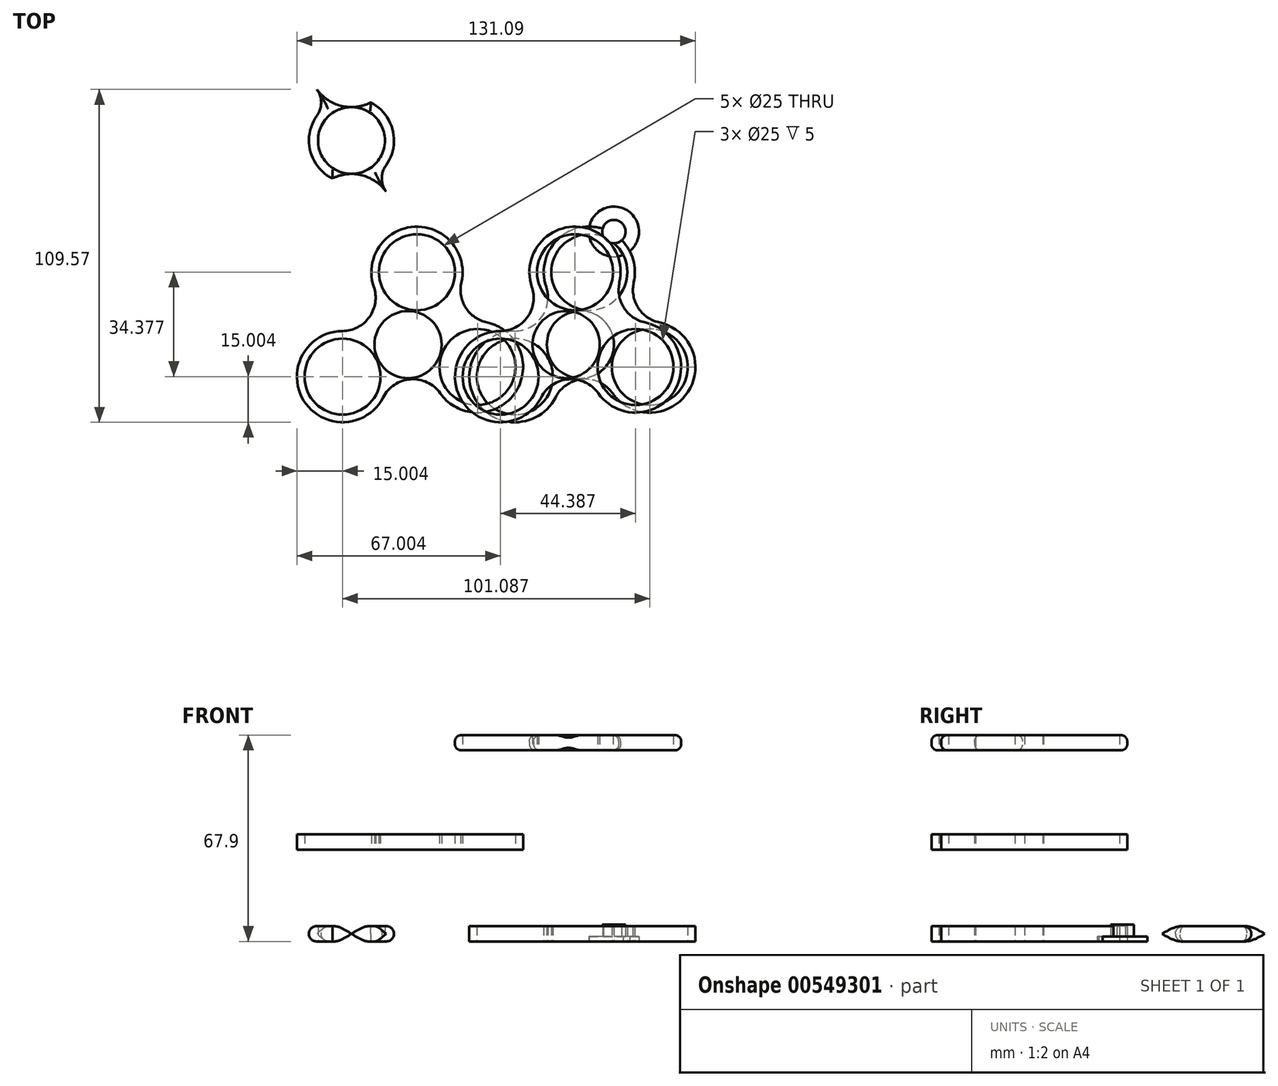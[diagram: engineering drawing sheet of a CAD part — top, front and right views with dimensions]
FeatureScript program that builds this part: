
annotation { "Feature Type Name" : "Feature", "Feature Type Description" : "" }
export const myFeature = defineFeature(function(context is Context, id is Id, definition is map)
    precondition{}
    {
        {
            var Q0;
            Q0=qCreatedBy(makeId("Top.planeOp"),FACE);
            var sketch = newSketch(context, id + "F0", { "sketchPlane" : qUnion([Q0])});
            skCircle(sketch, "E0", {"center": v(15.64, -42.07) * mm, "radius": 39 * mm});
            skCircle(sketch, "E1", {"center": v(15.64, -42.07) * mm, "radius": 11.05 * mm});
            skArc(sketch, "E2", {"start": v(15.64, -3.07) * mm, "mid": v(-17.23, -21.08) * mm, "end": v(-19.75, -58.47) * mm});
            skArc(sketch, "E3", {"start": v(-19.75, -58.47) * mm, "mid": v(14.6, -81.07) * mm, "end": v(50.1, -60.32) * mm});
            skLineSegment(sketch, "E4", {"start": v(-19.75, -58.47) * mm, "end": v(-17.55, -57.2) * mm});
            skLineSegment(sketch, "E5", {"start": v(15.64, -3.07) * mm, "end": v(16.72, -5.89) * mm});
            skLineSegment(sketch, "E6", {"start": v(50.1, -60.32) * mm, "end": v(47.05, -58.56) * mm});
            skCircle(sketch, "E7", {"center": v(18.57, -18.25) * mm, "radius": 12.5 * mm});
            skCircle(sketch, "E8", {"center": v(-5.92, -52.63) * mm, "radius": 12.5 * mm});
            skCircle(sketch, "E9", {"center": v(38.47, -49.46) * mm, "radius": 12.5 * mm});
            skCircle(sketch, "E10", {"center": v(18.57, -18.25) * mm, "radius": 15 * mm});
            skCircle(sketch, "E11", {"center": v(-5.92, -52.63) * mm, "radius": 15 * mm});
            skCircle(sketch, "E12", {"center": v(38.47, -49.46) * mm, "radius": 15 * mm});
            skPoint(sketch, "E13", {"position": v(15.64, -53.57) * mm});
            skPoint(sketch, "E14", {"position": v(3.28, -32.48) * mm});
            skPoint(sketch, "E15", {"position": v(34.2, -29.18) * mm});
            skArc(sketch, "E16", {"start": v(33.2, -21.6) * mm, "mid": v(34.64, -29.95) * mm, "end": v(41.6, -34.8) * mm});
            skArc(sketch, "E17", {"start": v(-5.98, -37.63) * mm, "mid": v(2.92, -33.01) * mm, "end": v(4.37, -23.09) * mm});
            skArc(sketch, "E18", {"start": v(26.21, -58.1) * mm, "mid": v(16.45, -53.48) * mm, "end": v(7.44, -59.45) * mm});
            skSolve(sketch);
        }
        {
            var Q0;
            {var subQ5=sQuery(id+"F0.wireOp",EDGE,"E16");Q0=makeQuery(id+"F0.imprint","IMPRINT",FACE,{"disambiguationData":[TD([[makeQuery(id+"F0.imprint","IMPRINT",EDGE,{"derivedFrom":subQ5}),-1.0]])]});}
            var Q1;
            Q1=makeQuery(id+"F0.imprint","IMPRINT",FACE,{"disambiguationData":[TD([[makeQuery(id+"F0.imprint","IMPRINT",EDGE,{"derivedFrom":sQuery(id+"F0.wireOp",EDGE,"E9")}),-1.0]])]});
            var Q2;
            {var subQ5=sQuery(id+"F0.wireOp",EDGE,"E18");Q2=makeQuery(id+"F0.imprint","IMPRINT",FACE,{"disambiguationData":[TD([[makeQuery(id+"F0.imprint","IMPRINT",EDGE,{"derivedFrom":subQ5}),-1.0]])]});}
            var Q3;
            Q3=makeQuery(id+"F0.imprint","IMPRINT",FACE,{"disambiguationData":[TD([[makeQuery(id+"F0.imprint","IMPRINT",EDGE,{"derivedFrom":sQuery(id+"F0.wireOp",EDGE,"E8")}),-1.0]])]});
            var Q4;
            {var subQ5=sQuery(id+"F0.wireOp",EDGE,"E17");Q4=makeQuery(id+"F0.imprint","IMPRINT",FACE,{"disambiguationData":[TD([[makeQuery(id+"F0.imprint","IMPRINT",EDGE,{"derivedFrom":subQ5}),-1.0]])]});}
            var Q5;
            Q5=makeQuery(id+"F0.imprint","IMPRINT",FACE,{"disambiguationData":[TD([[makeQuery(id+"F0.imprint","IMPRINT",EDGE,{"derivedFrom":sQuery(id+"F0.wireOp",EDGE,"E7")}),-1.0]])]});
            extrude(context, id + "F1", {"entities" : qUnion([Q0, Q1, Q2, Q3, Q4, Q5]), "depth" : 5 * mm, "offsetDistance" : 25 * mm});
        }
        {
            var Q0;
            Q0=qCreatedBy(makeId("Top.planeOp"),FACE);
            var sketch = newSketch(context, id + "F2", { "sketchPlane" : qUnion([Q0])});
            skLineSegment(sketch, "E19", {"start": v(-59.68, 64.11) * mm, "end": v(-59.68, -13.89) * mm});
            skLineSegment(sketch, "E20", {"start": v(-59.68, 64.11) * mm, "end": v(-59.68, 61.11) * mm});
            skLineSegment(sketch, "E21", {"start": v(-59.68, 61.11) * mm, "end": v(-59.68, 39.11) * mm});
            skLineSegment(sketch, "E22", {"start": v(-59.68, 39.11) * mm, "end": v(-59.68, 36.11) * mm});
            skLineSegment(sketch, "E23", {"start": v(-59.68, 36.11) * mm, "end": v(-59.68, 14.11) * mm});
            skLineSegment(sketch, "E24", {"start": v(-59.68, 14.11) * mm, "end": v(-59.68, 11.11) * mm});
            skLineSegment(sketch, "E25", {"start": v(-59.68, 11.11) * mm, "end": v(-59.68, -10.89) * mm});
            skLineSegment(sketch, "E26", {"start": v(-59.68, -10.89) * mm, "end": v(-59.68, -13.89) * mm});
            skCircle(sketch, "E27", {"center": v(-59.68, 25.11) * mm, "radius": 11 * mm});
            skCircle(sketch, "E28", {"center": v(-59.68, 0.11) * mm, "radius": 14 * mm});
            skCircle(sketch, "E29", {"center": v(-59.68, 25.11) * mm, "radius": 14 * mm});
            skCircle(sketch, "E30", {"center": v(-59.68, 50.11) * mm, "radius": 14 * mm});
            skArc(sketch, "E31", {"start": v(-48.31, 16.94) * mm, "mid": v(-49.7, 12.61) * mm, "end": v(-48.31, 8.28) * mm});
            skArc(sketch, "E32.MirrorCS", {"start": v(-71.05, 16.94) * mm, "mid": v(-69.66, 12.61) * mm, "end": v(-71.05, 8.28) * mm});
            skLineSegment(sketch, "E33", {"start": v(-70.68, 25.11) * mm, "end": v(-48.68, 25.11) * mm});
            skArc(sketch, "E34.MirrorCS", {"start": v(-48.31, 33.28) * mm, "mid": v(-49.7, 37.61) * mm, "end": v(-48.31, 41.94) * mm});
            skArc(sketch, "E35.MirrorCS", {"start": v(-71.05, 33.28) * mm, "mid": v(-69.66, 37.61) * mm, "end": v(-71.05, 41.94) * mm});
            skSolve(sketch);
        }
        {
            var Q0;
            {var subQ7=sQuery(id+"F2.wireOp",EDGE,"E20");Q0=makeQuery(id+"F2.imprint","IMPRINT",FACE,{"disambiguationData":[TD([[makeQuery(id+"F2.imprint","IMPRINT",EDGE,{"derivedFrom":subQ7}),1.0]])]});}
            var Q1;
            {var subQ0=sQuery(id+"F2.wireOp",EDGE,"E35.MirrorCS");Q1=makeQuery(id+"F2.imprint","IMPRINT",FACE,{"disambiguationData":[TD([[makeQuery(id+"F2.imprint","IMPRINT",EDGE,{"derivedFrom":subQ0}),-1.0]])]});}
            var Q2;
            {var subQ1=sQuery(id+"F2.wireOp",EDGE,"E20");Q2=makeQuery(id+"F2.imprint","IMPRINT",FACE,{"disambiguationData":[TD([[makeQuery(id+"F2.imprint","IMPRINT",EDGE,{"derivedFrom":subQ1}),-1.0]])]});}
            var Q3;
            {var subQ0=sQuery(id+"F2.wireOp",EDGE,"E22");Q3=makeQuery(id+"F2.imprint","IMPRINT",FACE,{"disambiguationData":[TD([[makeQuery(id+"F2.imprint","IMPRINT",EDGE,{"derivedFrom":subQ0}),-1.0]])]});}
            var Q4;
            {var subQ0=sQuery(id+"F2.wireOp",EDGE,"E22");Q4=makeQuery(id+"F2.imprint","IMPRINT",FACE,{"disambiguationData":[TD([[makeQuery(id+"F2.imprint","IMPRINT",EDGE,{"derivedFrom":subQ0}),1.0]])]});}
            var Q5;
            {var subQ0=sQuery(id+"F2.wireOp",EDGE,"E29");var subQ1=makeQuery(id+"F2.imprint","INTERSECT",VERTEX,{"derivedFrom":[subQ0,sQuery(id+"F2.wireOp",EDGE,"E34.MirrorCS")]});Q5=makeQuery(id+"F2.imprint","IMPRINT",FACE,{"disambiguationData":[TD([[makeQuery(id+"F2.imprint","IMPRINT",EDGE,{"disambiguationData":[TD([[subQ1,-1.0]])],"derivedFrom":subQ0}),1.0]])]});}
            var Q6;
            {var subQ0=sQuery(id+"F2.wireOp",EDGE,"E34.MirrorCS");Q6=makeQuery(id+"F2.imprint","IMPRINT",FACE,{"disambiguationData":[TD([[makeQuery(id+"F2.imprint","IMPRINT",EDGE,{"derivedFrom":subQ0}),1.0]])]});}
            var Q7;
            {var subQ0=sQuery(id+"F2.wireOp",EDGE,"E29");var subQ1=makeQuery(id+"F2.imprint","INTERSECT",VERTEX,{"derivedFrom":[subQ0,sQuery(id+"F2.wireOp",EDGE,"E35.MirrorCS")]});Q7=makeQuery(id+"F2.imprint","IMPRINT",FACE,{"disambiguationData":[TD([[makeQuery(id+"F2.imprint","IMPRINT",EDGE,{"disambiguationData":[TD([[subQ1,1.0]])],"derivedFrom":subQ0}),1.0]])]});}
            var Q8;
            {var subQ0=sQuery(id+"F2.wireOp",EDGE,"E24");Q8=makeQuery(id+"F2.imprint","IMPRINT",FACE,{"disambiguationData":[TD([[makeQuery(id+"F2.imprint","IMPRINT",EDGE,{"derivedFrom":subQ0}),-1.0]])]});}
            var Q9;
            {var subQ0=sQuery(id+"F2.wireOp",EDGE,"E24");Q9=makeQuery(id+"F2.imprint","IMPRINT",FACE,{"disambiguationData":[TD([[makeQuery(id+"F2.imprint","IMPRINT",EDGE,{"derivedFrom":subQ0}),1.0]])]});}
            var Q10;
            {var subQ0=sQuery(id+"F2.wireOp",EDGE,"E31");Q10=makeQuery(id+"F2.imprint","IMPRINT",FACE,{"disambiguationData":[TD([[makeQuery(id+"F2.imprint","IMPRINT",EDGE,{"derivedFrom":subQ0}),-1.0]])]});}
            var Q11;
            {var subQ1=sQuery(id+"F2.wireOp",EDGE,"E26");Q11=makeQuery(id+"F2.imprint","IMPRINT",FACE,{"disambiguationData":[TD([[makeQuery(id+"F2.imprint","IMPRINT",EDGE,{"derivedFrom":subQ1}),1.0]])]});}
            var Q12;
            {var subQ0=sQuery(id+"F2.wireOp",EDGE,"E32.MirrorCS");Q12=makeQuery(id+"F2.imprint","IMPRINT",FACE,{"disambiguationData":[TD([[makeQuery(id+"F2.imprint","IMPRINT",EDGE,{"derivedFrom":subQ0}),1.0]])]});}
            var Q13;
            {var subQ1=sQuery(id+"F2.wireOp",EDGE,"E26");Q13=makeQuery(id+"F2.imprint","IMPRINT",FACE,{"disambiguationData":[TD([[makeQuery(id+"F2.imprint","IMPRINT",EDGE,{"derivedFrom":subQ1}),-1.0]])]});}
            extrude(context, id + "F3", {"entities" : qUnion([Q0, Q1, Q2, Q3, Q4, Q5, Q6, Q7, Q8, Q9, Q10, Q11, Q12, Q13]), "depth" : 5 * mm, "offsetDistance" : 25 * mm});
        }
        {
            var Q0;
            Q0=makeQuery(id+"F3.opExtrude","CAP_EDGE",EDGE,{"disambiguationData":[OSD([sQuery(id+"F2.wireOp",EDGE,"E30")])],"isStart":false});
            var Q1;
            Q1=makeQuery(id+"F3.opExtrude","CAP_EDGE",EDGE,{"disambiguationData":[OSD([sQuery(id+"F2.wireOp",EDGE,"E35.MirrorCS")])],"isStart":false});
            var Q2;
            {var subQ0=sQuery(id+"F2.wireOp",EDGE,"E29");Q2=makeQuery(id+"F3.opExtrude","CAP_EDGE",EDGE,{"disambiguationData":[OSD([subQ0]),TDD([makeQuery(id+"F2.imprint","IMPRINT",EDGE,{"disambiguationData":[TD([[makeQuery(id+"F2.imprint","INTERSECT",VERTEX,{"derivedFrom":[subQ0,sQuery(id+"F2.wireOp",EDGE,"E32.MirrorCS")]}),1.0]])],"derivedFrom":subQ0})])],"isStart":false});}
            var Q3;
            Q3=makeQuery(id+"F3.opExtrude","CAP_EDGE",EDGE,{"disambiguationData":[OSD([sQuery(id+"F2.wireOp",EDGE,"E30")])],"isStart":true});
            var Q4;
            {var subQ0=sQuery(id+"F2.wireOp",EDGE,"E29");Q4=makeQuery(id+"F3.opExtrude","CAP_EDGE",EDGE,{"disambiguationData":[OSD([subQ0]),TDD([makeQuery(id+"F2.imprint","IMPRINT",EDGE,{"disambiguationData":[TD([[makeQuery(id+"F2.imprint","INTERSECT",VERTEX,{"derivedFrom":[subQ0,sQuery(id+"F2.wireOp",EDGE,"E31")]}),-1.0]])],"derivedFrom":subQ0})])],"isStart":true});}
            var Q5;
            Q5=makeQuery(id+"F3.opExtrude","CAP_EDGE",EDGE,{"disambiguationData":[OSD([sQuery(id+"F2.wireOp",EDGE,"E31")])],"isStart":true});
            var Q6;
            Q6=makeQuery(id+"F3.opExtrude","CAP_EDGE",EDGE,{"disambiguationData":[OSD([sQuery(id+"F2.wireOp",EDGE,"E28")])],"isStart":true});
            var Q7;
            Q7=makeQuery(id+"F3.opExtrude","CAP_EDGE",EDGE,{"disambiguationData":[OSD([sQuery(id+"F2.wireOp",EDGE,"E32.MirrorCS")])],"isStart":true});
            var Q8;
            {var subQ0=sQuery(id+"F2.wireOp",EDGE,"E29");Q8=makeQuery(id+"F3.opExtrude","CAP_EDGE",EDGE,{"disambiguationData":[OSD([subQ0]),TDD([makeQuery(id+"F2.imprint","IMPRINT",EDGE,{"disambiguationData":[TD([[makeQuery(id+"F2.imprint","INTERSECT",VERTEX,{"derivedFrom":[subQ0,sQuery(id+"F2.wireOp",EDGE,"E32.MirrorCS")]}),1.0]])],"derivedFrom":subQ0})])],"isStart":true});}
            var Q9;
            Q9=makeQuery(id+"F3.opExtrude","CAP_EDGE",EDGE,{"disambiguationData":[OSD([sQuery(id+"F2.wireOp",EDGE,"E35.MirrorCS")])],"isStart":true});
            var Q10;
            Q10=makeQuery(id+"F3.opExtrude","CAP_EDGE",EDGE,{"disambiguationData":[OSD([sQuery(id+"F2.wireOp",EDGE,"E34.MirrorCS")])],"isStart":true});
            var Q11;
            Q11=makeQuery(id+"F3.opExtrude","CAP_EDGE",EDGE,{"disambiguationData":[OSD([sQuery(id+"F2.wireOp",EDGE,"E34.MirrorCS")])],"isStart":false});
            var Q12;
            {var subQ0=sQuery(id+"F2.wireOp",EDGE,"E29");Q12=makeQuery(id+"F3.opExtrude","CAP_EDGE",EDGE,{"disambiguationData":[OSD([subQ0]),TDD([makeQuery(id+"F2.imprint","IMPRINT",EDGE,{"disambiguationData":[TD([[makeQuery(id+"F2.imprint","INTERSECT",VERTEX,{"derivedFrom":[subQ0,sQuery(id+"F2.wireOp",EDGE,"E31")]}),-1.0]])],"derivedFrom":subQ0})])],"isStart":false});}
            var Q13;
            Q13=makeQuery(id+"F3.opExtrude","CAP_EDGE",EDGE,{"disambiguationData":[OSD([sQuery(id+"F2.wireOp",EDGE,"E31")])],"isStart":false});
            var Q14;
            Q14=makeQuery(id+"F3.opExtrude","CAP_EDGE",EDGE,{"disambiguationData":[OSD([sQuery(id+"F2.wireOp",EDGE,"E28")])],"isStart":false});
            var Q15;
            Q15=makeQuery(id+"F3.opExtrude","CAP_EDGE",EDGE,{"disambiguationData":[OSD([sQuery(id+"F2.wireOp",EDGE,"E32.MirrorCS")])],"isStart":false});
            fillet(context, id + "F4", {"entities" : qUnion([Q0, Q1, Q2, Q3, Q4, Q5, Q6, Q7, Q8, Q9, Q10, Q11, Q12, Q13, Q14, Q15]), "radius" : 2.5 * mm, "tangentPropagation" : true, "allowEdgeOverflow" : false});
        }
        {
            var Q0;
            Q0=makeQuery(id+"F1.opExtrude","SWEPT_BODY",BODY,{"disambiguationData":[OSD([sQuery(id+"F0.wireOp",EDGE,"E1"),sQuery(id+"F0.wireOp",EDGE,"E7"),sQuery(id+"F0.wireOp",EDGE,"E8"),sQuery(id+"F0.wireOp",EDGE,"E9"),sQuery(id+"F0.wireOp",EDGE,"E10"),sQuery(id+"F0.wireOp",EDGE,"E11"),sQuery(id+"F0.wireOp",EDGE,"E12"),sQuery(id+"F0.wireOp",EDGE,"E16"),sQuery(id+"F0.wireOp",EDGE,"E17"),sQuery(id+"F0.wireOp",EDGE,"E18")])]});
            transform(context, id + "F5", {"entities" : qUnion([Q0]), "transformType" : TransformType.TRANSLATION_3D, "dx" : -4.7 * mm, "dy" : 0 * mm, "dz" : 62.9 * mm, "makeCopy" : true});
        }
        {
            var Q0;
            Q0=makeQuery(id+"F5.opPattern","COPY",BODY,{"derivedFrom":makeQuery(id+"F1.opExtrude","SWEPT_BODY",BODY,{"disambiguationData":[OSD([sQuery(id+"F0.wireOp",EDGE,"E1"),sQuery(id+"F0.wireOp",EDGE,"E7"),sQuery(id+"F0.wireOp",EDGE,"E8"),sQuery(id+"F0.wireOp",EDGE,"E9"),sQuery(id+"F0.wireOp",EDGE,"E10"),sQuery(id+"F0.wireOp",EDGE,"E11"),sQuery(id+"F0.wireOp",EDGE,"E12"),sQuery(id+"F0.wireOp",EDGE,"E16"),sQuery(id+"F0.wireOp",EDGE,"E17"),sQuery(id+"F0.wireOp",EDGE,"E18")])]}),"instanceName":"1"});
            transform(context, id + "F6", {"entities" : qUnion([Q0]), "transformType" : TransformType.TRANSLATION_3D, "dx" : -52 * mm, "dy" : 0 * mm, "dz" : -32.7 * mm, "makeCopy" : true});
        }
        {
            var Q0;
            Q0=qCreatedBy(makeId("Top.planeOp"),FACE);
            var sketch = newSketch(context, id + "F7", { "sketchPlane" : qUnion([Q0])});
            skCircle(sketch, "E36", {"center": v(26.66, -4.88) * mm, "radius": 8.25 * mm});
            skSolve(sketch);
        }
        {
            var Q0;
            Q0=makeQuery(id+"F7.imprint","IMPRINT",FACE,{"disambiguationData":[TD([[makeQuery(id+"F7.imprint","IMPRINT",EDGE,{"derivedFrom":sQuery(id+"F7.wireOp",EDGE,"E36")}),1.0]])]});
            extrude(context, id + "F8", {"entities" : qUnion([Q0]), "depth" : 1.64 * mm, "offsetDistance" : 25 * mm});
        }
        {
            var Q0;
            Q0=makeQuery(id+"F8.opExtrude","CAP_FACE",FACE,{"disambiguationData":[OSD([sQuery(id+"F7.wireOp",EDGE,"E36")])],"isStart":false});
            var sketch = newSketch(context, id + "F9", { "sketchPlane" : qUnion([Q0])});
            skCircle(sketch, "E37", {"center": v(26.66, -4.88) * mm, "radius": 3.84 * mm});
            skSolve(sketch);
        }
        {
            var Q0;
            Q0=makeQuery(id+"F9.imprint","IMPRINT",FACE,{"disambiguationData":[TD([[makeQuery(id+"F9.imprint","IMPRINT",EDGE,{"derivedFrom":sQuery(id+"F9.wireOp",EDGE,"E37")}),1.0]])]});
            extrude(context, id + "F10", {"entities" : qUnion([Q0]), "operationType" : NewBodyOperationType.ADD, "depth" : 3.9 * mm, "offsetDistance" : 25 * mm});
        }
        {
            var Q0;
            Q0=makeQuery(id+"F3.opExtrude","CAP_FACE",FACE,{"disambiguationData":[OSD([sQuery(id+"F2.wireOp",EDGE,"E27"),sQuery(id+"F2.wireOp",EDGE,"E28"),sQuery(id+"F2.wireOp",EDGE,"E29"),sQuery(id+"F2.wireOp",EDGE,"E30"),sQuery(id+"F2.wireOp",EDGE,"E31"),sQuery(id+"F2.wireOp",EDGE,"E32.MirrorCS"),sQuery(id+"F2.wireOp",EDGE,"E34.MirrorCS"),sQuery(id+"F2.wireOp",EDGE,"E35.MirrorCS")])],"isStart":false});
            var sketch = newSketch(context, id + "F11", { "sketchPlane" : qUnion([Q0])});
            skLineSegment(sketch, "E38", {"start": v(-59.97, -1.73) * mm, "end": v(-62.66, -1.73) * mm});
            skLineSegment(sketch, "E39", {"start": v(-62.66, -1.73) * mm, "end": v(-62.7, -1.73) * mm});
            skLineSegment(sketch, "E40", {"start": v(-62.7, -1.73) * mm, "end": v(-62.8, -1.76) * mm});
            skLineSegment(sketch, "E41", {"start": v(-62.8, -1.76) * mm, "end": v(-62.93, -1.84) * mm});
            skLineSegment(sketch, "E42", {"start": v(-62.93, -1.84) * mm, "end": v(-63, -1.95) * mm});
            skLineSegment(sketch, "E43", {"start": v(-63, -1.95) * mm, "end": v(-63.04, -2.06) * mm});
            skLineSegment(sketch, "E44", {"start": v(-63.04, -2.06) * mm, "end": v(-63.04, -2.1) * mm});
            skLineSegment(sketch, "E45", {"start": v(-63.04, -2.1) * mm, "end": v(-63.04, -2.14) * mm});
            skLineSegment(sketch, "E46", {"start": v(-63.04, -2.14) * mm, "end": v(-63, -2.24) * mm});
            skLineSegment(sketch, "E47", {"start": v(-63, -2.24) * mm, "end": v(-62.93, -2.36) * mm});
            skLineSegment(sketch, "E48", {"start": v(-62.93, -2.36) * mm, "end": v(-62.8, -2.44) * mm});
            skLineSegment(sketch, "E49", {"start": v(-62.8, -2.44) * mm, "end": v(-62.7, -2.47) * mm});
            skLineSegment(sketch, "E50", {"start": v(-62.7, -2.47) * mm, "end": v(-62.66, -2.47) * mm});
            skLineSegment(sketch, "E51", {"start": v(-62.66, -2.47) * mm, "end": v(-59.97, -2.47) * mm});
            skLineSegment(sketch, "E52", {"start": v(-59.97, -2.47) * mm, "end": v(-59.93, -2.47) * mm});
            skLineSegment(sketch, "E53", {"start": v(-59.93, -2.47) * mm, "end": v(-59.82, -2.44) * mm});
            skLineSegment(sketch, "E54", {"start": v(-59.82, -2.44) * mm, "end": v(-59.7, -2.36) * mm});
            skLineSegment(sketch, "E55", {"start": v(-59.7, -2.36) * mm, "end": v(-59.63, -2.24) * mm});
            skLineSegment(sketch, "E56", {"start": v(-59.63, -2.24) * mm, "end": v(-59.6, -2.14) * mm});
            skLineSegment(sketch, "E57", {"start": v(-59.6, -2.14) * mm, "end": v(-59.6, -2.1) * mm});
            skLineSegment(sketch, "E58", {"start": v(-59.6, -2.1) * mm, "end": v(-59.6, -2.06) * mm});
            skLineSegment(sketch, "E59", {"start": v(-59.6, -2.06) * mm, "end": v(-59.63, -1.95) * mm});
            skLineSegment(sketch, "E60", {"start": v(-59.63, -1.95) * mm, "end": v(-59.7, -1.84) * mm});
            skLineSegment(sketch, "E61", {"start": v(-59.7, -1.84) * mm, "end": v(-59.82, -1.76) * mm});
            skLineSegment(sketch, "E62", {"start": v(-59.82, -1.76) * mm, "end": v(-59.93, -1.73) * mm});
            skLineSegment(sketch, "E63", {"start": v(-59.93, -1.73) * mm, "end": v(-59.97, -1.73) * mm});
            skLineSegment(sketch, "E64", {"start": v(-58.26, -0.47) * mm, "end": v(-62.14, -0.47) * mm});
            skLineSegment(sketch, "E65", {"start": v(-62.14, -0.47) * mm, "end": v(-62.17, -0.47) * mm});
            skLineSegment(sketch, "E66", {"start": v(-62.17, -0.47) * mm, "end": v(-62.28, -0.5) * mm});
            skLineSegment(sketch, "E67", {"start": v(-62.28, -0.5) * mm, "end": v(-62.4, -0.58) * mm});
            skLineSegment(sketch, "E68", {"start": v(-62.4, -0.58) * mm, "end": v(-62.48, -0.7) * mm});
            skLineSegment(sketch, "E69", {"start": v(-62.48, -0.7) * mm, "end": v(-62.5, -0.8) * mm});
            skLineSegment(sketch, "E70", {"start": v(-62.5, -0.8) * mm, "end": v(-62.5, -0.84) * mm});
            skLineSegment(sketch, "E71", {"start": v(-62.5, -0.84) * mm, "end": v(-62.5, -0.88) * mm});
            skLineSegment(sketch, "E72", {"start": v(-62.5, -0.88) * mm, "end": v(-62.48, -0.98) * mm});
            skLineSegment(sketch, "E73", {"start": v(-62.48, -0.98) * mm, "end": v(-62.4, -1.1) * mm});
            skLineSegment(sketch, "E74", {"start": v(-62.4, -1.1) * mm, "end": v(-62.28, -1.18) * mm});
            skLineSegment(sketch, "E75", {"start": v(-62.28, -1.18) * mm, "end": v(-62.17, -1.21) * mm});
            skLineSegment(sketch, "E76", {"start": v(-62.17, -1.21) * mm, "end": v(-62.14, -1.21) * mm});
            skLineSegment(sketch, "E77", {"start": v(-62.14, -1.21) * mm, "end": v(-58.26, -1.21) * mm});
            skLineSegment(sketch, "E78", {"start": v(-58.26, -1.21) * mm, "end": v(-58.22, -1.21) * mm});
            skLineSegment(sketch, "E79", {"start": v(-58.22, -1.21) * mm, "end": v(-58.11, -1.18) * mm});
            skLineSegment(sketch, "E80", {"start": v(-58.11, -1.18) * mm, "end": v(-58, -1.1) * mm});
            skLineSegment(sketch, "E81", {"start": v(-58, -1.1) * mm, "end": v(-57.91, -0.98) * mm});
            skLineSegment(sketch, "E82", {"start": v(-57.91, -0.98) * mm, "end": v(-57.88, -0.88) * mm});
            skLineSegment(sketch, "E83", {"start": v(-57.88, -0.88) * mm, "end": v(-57.88, -0.84) * mm});
            skLineSegment(sketch, "E84", {"start": v(-57.88, -0.84) * mm, "end": v(-57.88, -0.8) * mm});
            skLineSegment(sketch, "E85", {"start": v(-57.88, -0.8) * mm, "end": v(-57.91, -0.7) * mm});
            skLineSegment(sketch, "E86", {"start": v(-57.91, -0.7) * mm, "end": v(-58, -0.58) * mm});
            skLineSegment(sketch, "E87", {"start": v(-58, -0.58) * mm, "end": v(-58.11, -0.5) * mm});
            skLineSegment(sketch, "E88", {"start": v(-58.11, -0.5) * mm, "end": v(-58.22, -0.47) * mm});
            skLineSegment(sketch, "E89", {"start": v(-58.22, -0.47) * mm, "end": v(-58.26, -0.47) * mm});
            skLineSegment(sketch, "E90", {"start": v(-57.47, 0.8) * mm, "end": v(-62.14, 0.8) * mm});
            skLineSegment(sketch, "E91", {"start": v(-62.14, 0.8) * mm, "end": v(-62.17, 0.8) * mm});
            skLineSegment(sketch, "E92", {"start": v(-62.17, 0.8) * mm, "end": v(-62.28, 0.76) * mm});
            skLineSegment(sketch, "E93", {"start": v(-62.28, 0.76) * mm, "end": v(-62.4, 0.68) * mm});
            skLineSegment(sketch, "E94", {"start": v(-62.4, 0.68) * mm, "end": v(-62.48, 0.57) * mm});
            skLineSegment(sketch, "E95", {"start": v(-62.48, 0.57) * mm, "end": v(-62.5, 0.46) * mm});
            skLineSegment(sketch, "E96", {"start": v(-62.5, 0.46) * mm, "end": v(-62.5, 0.42) * mm});
            skLineSegment(sketch, "E97", {"start": v(-62.5, 0.42) * mm, "end": v(-62.5, 0.38) * mm});
            skLineSegment(sketch, "E98", {"start": v(-62.5, 0.38) * mm, "end": v(-62.48, 0.28) * mm});
            skLineSegment(sketch, "E99", {"start": v(-62.48, 0.28) * mm, "end": v(-62.4, 0.16) * mm});
            skLineSegment(sketch, "E100", {"start": v(-62.4, 0.16) * mm, "end": v(-62.28, 0.08) * mm});
            skLineSegment(sketch, "E101", {"start": v(-62.28, 0.08) * mm, "end": v(-62.17, 0.05) * mm});
            skLineSegment(sketch, "E102", {"start": v(-62.17, 0.05) * mm, "end": v(-62.14, 0.05) * mm});
            skLineSegment(sketch, "E103", {"start": v(-62.14, 0.05) * mm, "end": v(-57.47, 0.05) * mm});
            skLineSegment(sketch, "E104", {"start": v(-57.47, 0.05) * mm, "end": v(-57.43, 0.05) * mm});
            skLineSegment(sketch, "E105", {"start": v(-57.43, 0.05) * mm, "end": v(-57.32, 0.08) * mm});
            skLineSegment(sketch, "E106", {"start": v(-57.32, 0.08) * mm, "end": v(-57.2, 0.16) * mm});
            skLineSegment(sketch, "E107", {"start": v(-57.2, 0.16) * mm, "end": v(-57.13, 0.28) * mm});
            skLineSegment(sketch, "E108", {"start": v(-57.13, 0.28) * mm, "end": v(-57.1, 0.38) * mm});
            skLineSegment(sketch, "E109", {"start": v(-57.1, 0.38) * mm, "end": v(-57.1, 0.42) * mm});
            skLineSegment(sketch, "E110", {"start": v(-57.1, 0.42) * mm, "end": v(-57.1, 0.46) * mm});
            skLineSegment(sketch, "E111", {"start": v(-57.1, 0.46) * mm, "end": v(-57.13, 0.57) * mm});
            skLineSegment(sketch, "E112", {"start": v(-57.13, 0.57) * mm, "end": v(-57.2, 0.68) * mm});
            skLineSegment(sketch, "E113", {"start": v(-57.2, 0.68) * mm, "end": v(-57.32, 0.76) * mm});
            skLineSegment(sketch, "E114", {"start": v(-57.32, 0.76) * mm, "end": v(-57.43, 0.8) * mm});
            skLineSegment(sketch, "E115", {"start": v(-57.43, 0.8) * mm, "end": v(-57.47, 0.8) * mm});
            skLineSegment(sketch, "E116", {"start": v(-58.11, 2.05) * mm, "end": v(-62.14, 2.05) * mm});
            skLineSegment(sketch, "E117", {"start": v(-62.14, 2.05) * mm, "end": v(-62.17, 2.05) * mm});
            skLineSegment(sketch, "E118", {"start": v(-62.17, 2.05) * mm, "end": v(-62.28, 2.02) * mm});
            skLineSegment(sketch, "E119", {"start": v(-62.28, 2.02) * mm, "end": v(-62.4, 1.94) * mm});
            skLineSegment(sketch, "E120", {"start": v(-62.4, 1.94) * mm, "end": v(-62.48, 1.82) * mm});
            skLineSegment(sketch, "E121", {"start": v(-62.48, 1.82) * mm, "end": v(-62.5, 1.72) * mm});
            skLineSegment(sketch, "E122", {"start": v(-62.5, 1.72) * mm, "end": v(-62.5, 1.68) * mm});
            skLineSegment(sketch, "E123", {"start": v(-62.5, 1.68) * mm, "end": v(-62.5, 1.64) * mm});
            skLineSegment(sketch, "E124", {"start": v(-62.5, 1.64) * mm, "end": v(-62.48, 1.53) * mm});
            skLineSegment(sketch, "E125", {"start": v(-62.48, 1.53) * mm, "end": v(-62.4, 1.42) * mm});
            skLineSegment(sketch, "E126", {"start": v(-62.4, 1.42) * mm, "end": v(-62.28, 1.34) * mm});
            skLineSegment(sketch, "E127", {"start": v(-62.28, 1.34) * mm, "end": v(-62.17, 1.3) * mm});
            skLineSegment(sketch, "E128", {"start": v(-62.17, 1.3) * mm, "end": v(-62.14, 1.3) * mm});
            skLineSegment(sketch, "E129", {"start": v(-62.14, 1.3) * mm, "end": v(-58.11, 1.3) * mm});
            skLineSegment(sketch, "E130", {"start": v(-58.11, 1.3) * mm, "end": v(-58.08, 1.3) * mm});
            skLineSegment(sketch, "E131", {"start": v(-58.08, 1.3) * mm, "end": v(-57.97, 1.34) * mm});
            skLineSegment(sketch, "E132", {"start": v(-57.97, 1.34) * mm, "end": v(-57.85, 1.42) * mm});
            skLineSegment(sketch, "E133", {"start": v(-57.85, 1.42) * mm, "end": v(-57.77, 1.53) * mm});
            skLineSegment(sketch, "E134", {"start": v(-57.77, 1.53) * mm, "end": v(-57.74, 1.64) * mm});
            skLineSegment(sketch, "E135", {"start": v(-57.74, 1.64) * mm, "end": v(-57.74, 1.68) * mm});
            skLineSegment(sketch, "E136", {"start": v(-57.74, 1.68) * mm, "end": v(-57.74, 1.72) * mm});
            skLineSegment(sketch, "E137", {"start": v(-57.74, 1.72) * mm, "end": v(-57.77, 1.82) * mm});
            skLineSegment(sketch, "E138", {"start": v(-57.77, 1.82) * mm, "end": v(-57.85, 1.94) * mm});
            skLineSegment(sketch, "E139", {"start": v(-57.85, 1.94) * mm, "end": v(-57.97, 2.02) * mm});
            skLineSegment(sketch, "E140", {"start": v(-57.97, 2.02) * mm, "end": v(-58.08, 2.05) * mm});
            skLineSegment(sketch, "E141", {"start": v(-58.08, 2.05) * mm, "end": v(-58.11, 2.05) * mm});
            skLineSegment(sketch, "E142", {"start": v(-61.54, 3.31) * mm, "end": v(-62.66, 3.31) * mm});
            skLineSegment(sketch, "E143", {"start": v(-62.66, 3.31) * mm, "end": v(-62.7, 3.31) * mm});
            skLineSegment(sketch, "E144", {"start": v(-62.7, 3.31) * mm, "end": v(-62.8, 3.28) * mm});
            skLineSegment(sketch, "E145", {"start": v(-62.8, 3.28) * mm, "end": v(-62.93, 3.2) * mm});
            skLineSegment(sketch, "E146", {"start": v(-62.93, 3.2) * mm, "end": v(-63, 3.08) * mm});
            skLineSegment(sketch, "E147", {"start": v(-63, 3.08) * mm, "end": v(-63.04, 2.98) * mm});
            skLineSegment(sketch, "E148", {"start": v(-63.04, 2.98) * mm, "end": v(-63.04, 2.94) * mm});
            skLineSegment(sketch, "E149", {"start": v(-63.04, 2.94) * mm, "end": v(-63.04, 2.9) * mm});
            skLineSegment(sketch, "E150", {"start": v(-63.04, 2.9) * mm, "end": v(-63, 2.8) * mm});
            skLineSegment(sketch, "E151", {"start": v(-63, 2.8) * mm, "end": v(-62.93, 2.68) * mm});
            skLineSegment(sketch, "E152", {"start": v(-62.93, 2.68) * mm, "end": v(-62.8, 2.6) * mm});
            skLineSegment(sketch, "E153", {"start": v(-62.8, 2.6) * mm, "end": v(-62.7, 2.57) * mm});
            skLineSegment(sketch, "E154", {"start": v(-62.7, 2.57) * mm, "end": v(-62.66, 2.57) * mm});
            skLineSegment(sketch, "E155", {"start": v(-62.66, 2.57) * mm, "end": v(-61.54, 2.57) * mm});
            skLineSegment(sketch, "E156", {"start": v(-61.54, 2.57) * mm, "end": v(-61.5, 2.57) * mm});
            skLineSegment(sketch, "E157", {"start": v(-61.5, 2.57) * mm, "end": v(-61.4, 2.6) * mm});
            skLineSegment(sketch, "E158", {"start": v(-61.4, 2.6) * mm, "end": v(-61.28, 2.68) * mm});
            skLineSegment(sketch, "E159", {"start": v(-61.28, 2.68) * mm, "end": v(-61.2, 2.8) * mm});
            skLineSegment(sketch, "E160", {"start": v(-61.2, 2.8) * mm, "end": v(-61.17, 2.9) * mm});
            skLineSegment(sketch, "E161", {"start": v(-61.17, 2.9) * mm, "end": v(-61.17, 2.94) * mm});
            skLineSegment(sketch, "E162", {"start": v(-61.17, 2.94) * mm, "end": v(-61.17, 2.98) * mm});
            skLineSegment(sketch, "E163", {"start": v(-61.17, 2.98) * mm, "end": v(-61.2, 3.08) * mm});
            skLineSegment(sketch, "E164", {"start": v(-61.2, 3.08) * mm, "end": v(-61.28, 3.2) * mm});
            skLineSegment(sketch, "E165", {"start": v(-61.28, 3.2) * mm, "end": v(-61.4, 3.28) * mm});
            skLineSegment(sketch, "E166", {"start": v(-61.4, 3.28) * mm, "end": v(-61.5, 3.31) * mm});
            skLineSegment(sketch, "E167", {"start": v(-61.5, 3.31) * mm, "end": v(-61.54, 3.31) * mm});
            skLineSegment(sketch, "E168", {"start": v(-62.92, 5) * mm, "end": v(-63, 5) * mm});
            skLineSegment(sketch, "E169", {"start": v(-63, 5) * mm, "end": v(-63.22, 4.96) * mm});
            skLineSegment(sketch, "E170", {"start": v(-63.22, 4.96) * mm, "end": v(-63.5, 4.87) * mm});
            skLineSegment(sketch, "E171", {"start": v(-63.5, 4.87) * mm, "end": v(-63.76, 4.73) * mm});
            skLineSegment(sketch, "E172", {"start": v(-63.76, 4.73) * mm, "end": v(-63.98, 4.55) * mm});
            skLineSegment(sketch, "E173", {"start": v(-63.98, 4.55) * mm, "end": v(-64.17, 4.33) * mm});
            skLineSegment(sketch, "E174", {"start": v(-64.17, 4.33) * mm, "end": v(-64.3, 4.07) * mm});
            skLineSegment(sketch, "E175", {"start": v(-64.3, 4.07) * mm, "end": v(-64.4, 3.79) * mm});
            skLineSegment(sketch, "E176", {"start": v(-64.4, 3.79) * mm, "end": v(-64.43, 3.56) * mm});
            skLineSegment(sketch, "E177", {"start": v(-64.43, 3.56) * mm, "end": v(-64.43, 3.48) * mm});
            skLineSegment(sketch, "E178", {"start": v(-64.43, 3.48) * mm, "end": v(-64.43, -2.7) * mm});
            skLineSegment(sketch, "E179", {"start": v(-64.43, -2.7) * mm, "end": v(-64.43, -2.77) * mm});
            skLineSegment(sketch, "E180", {"start": v(-64.43, -2.77) * mm, "end": v(-64.4, -3) * mm});
            skLineSegment(sketch, "E181", {"start": v(-64.4, -3) * mm, "end": v(-64.3, -3.28) * mm});
            skLineSegment(sketch, "E182", {"start": v(-64.3, -3.28) * mm, "end": v(-64.17, -3.53) * mm});
            skLineSegment(sketch, "E183", {"start": v(-64.17, -3.53) * mm, "end": v(-63.98, -3.76) * mm});
            skLineSegment(sketch, "E184", {"start": v(-63.98, -3.76) * mm, "end": v(-63.76, -3.94) * mm});
            skLineSegment(sketch, "E185", {"start": v(-63.76, -3.94) * mm, "end": v(-63.5, -4.08) * mm});
            skLineSegment(sketch, "E186", {"start": v(-63.5, -4.08) * mm, "end": v(-63.22, -4.17) * mm});
            skLineSegment(sketch, "E187", {"start": v(-63.22, -4.17) * mm, "end": v(-63, -4.2) * mm});
            skLineSegment(sketch, "E188", {"start": v(-63, -4.2) * mm, "end": v(-62.92, -4.2) * mm});
            skLineSegment(sketch, "E189", {"start": v(-62.92, -4.2) * mm, "end": v(-55.62, -4.2) * mm});
            skLineSegment(sketch, "E190", {"start": v(-55.62, -4.2) * mm, "end": v(-55.59, -4.2) * mm});
            skLineSegment(sketch, "E191", {"start": v(-55.59, -4.2) * mm, "end": v(-55.47, -4.17) * mm});
            skLineSegment(sketch, "E192", {"start": v(-55.47, -4.17) * mm, "end": v(-55.35, -4.09) * mm});
            skLineSegment(sketch, "E193", {"start": v(-55.35, -4.09) * mm, "end": v(-55.27, -3.96) * mm});
            skLineSegment(sketch, "E194", {"start": v(-55.27, -3.96) * mm, "end": v(-55.23, -3.85) * mm});
            skLineSegment(sketch, "E195", {"start": v(-55.23, -3.85) * mm, "end": v(-55.23, -3.81) * mm});
            skLineSegment(sketch, "E196", {"start": v(-55.23, -3.81) * mm, "end": v(-55.23, -3.77) * mm});
            skLineSegment(sketch, "E197", {"start": v(-55.23, -3.77) * mm, "end": v(-55.27, -3.66) * mm});
            skLineSegment(sketch, "E198", {"start": v(-55.27, -3.66) * mm, "end": v(-55.35, -3.53) * mm});
            skLineSegment(sketch, "E199", {"start": v(-55.35, -3.53) * mm, "end": v(-55.47, -3.45) * mm});
            skLineSegment(sketch, "E200", {"start": v(-55.47, -3.45) * mm, "end": v(-55.59, -3.42) * mm});
            skLineSegment(sketch, "E201", {"start": v(-55.59, -3.42) * mm, "end": v(-55.62, -3.42) * mm});
            skLineSegment(sketch, "E202", {"start": v(-55.62, -3.42) * mm, "end": v(-62.92, -3.42) * mm});
            skLineSegment(sketch, "E203", {"start": v(-62.92, -3.42) * mm, "end": v(-62.95, -3.42) * mm});
            skLineSegment(sketch, "E204", {"start": v(-62.95, -3.42) * mm, "end": v(-63.06, -3.4) * mm});
            skLineSegment(sketch, "E205", {"start": v(-63.06, -3.4) * mm, "end": v(-63.2, -3.36) * mm});
            skLineSegment(sketch, "E206", {"start": v(-63.2, -3.36) * mm, "end": v(-63.32, -3.3) * mm});
            skLineSegment(sketch, "E207", {"start": v(-63.32, -3.3) * mm, "end": v(-63.43, -3.2) * mm});
            skLineSegment(sketch, "E208", {"start": v(-63.43, -3.2) * mm, "end": v(-63.52, -3.1) * mm});
            skLineSegment(sketch, "E209", {"start": v(-63.52, -3.1) * mm, "end": v(-63.59, -2.97) * mm});
            skLineSegment(sketch, "E210", {"start": v(-63.59, -2.97) * mm, "end": v(-63.63, -2.84) * mm});
            skLineSegment(sketch, "E211", {"start": v(-63.63, -2.84) * mm, "end": v(-63.65, -2.73) * mm});
            skLineSegment(sketch, "E212", {"start": v(-63.65, -2.73) * mm, "end": v(-63.65, -2.7) * mm});
            skLineSegment(sketch, "E213", {"start": v(-63.65, -2.7) * mm, "end": v(-63.65, 3.48) * mm});
            skLineSegment(sketch, "E214", {"start": v(-63.65, 3.48) * mm, "end": v(-63.65, 3.52) * mm});
            skLineSegment(sketch, "E215", {"start": v(-63.65, 3.52) * mm, "end": v(-63.63, 3.63) * mm});
            skLineSegment(sketch, "E216", {"start": v(-63.63, 3.63) * mm, "end": v(-63.59, 3.77) * mm});
            skLineSegment(sketch, "E217", {"start": v(-63.59, 3.77) * mm, "end": v(-63.52, 3.89) * mm});
            skLineSegment(sketch, "E218", {"start": v(-63.52, 3.89) * mm, "end": v(-63.43, 4) * mm});
            skLineSegment(sketch, "E219", {"start": v(-63.43, 4) * mm, "end": v(-63.32, 4.09) * mm});
            skLineSegment(sketch, "E220", {"start": v(-63.32, 4.09) * mm, "end": v(-63.2, 4.15) * mm});
            skLineSegment(sketch, "E221", {"start": v(-63.2, 4.15) * mm, "end": v(-63.06, 4.2) * mm});
            skLineSegment(sketch, "E222", {"start": v(-63.06, 4.2) * mm, "end": v(-62.95, 4.21) * mm});
            skLineSegment(sketch, "E223", {"start": v(-62.95, 4.21) * mm, "end": v(-62.92, 4.21) * mm});
            skLineSegment(sketch, "E224", {"start": v(-62.92, 4.21) * mm, "end": v(-56.74, 4.21) * mm});
            skLineSegment(sketch, "E225", {"start": v(-56.74, 4.21) * mm, "end": v(-56.7, 4.21) * mm});
            skLineSegment(sketch, "E226", {"start": v(-56.7, 4.21) * mm, "end": v(-56.6, 4.2) * mm});
            skLineSegment(sketch, "E227", {"start": v(-56.6, 4.2) * mm, "end": v(-56.46, 4.15) * mm});
            skLineSegment(sketch, "E228", {"start": v(-56.46, 4.15) * mm, "end": v(-56.34, 4.09) * mm});
            skLineSegment(sketch, "E229", {"start": v(-56.34, 4.09) * mm, "end": v(-56.23, 4) * mm});
            skLineSegment(sketch, "E230", {"start": v(-56.23, 4) * mm, "end": v(-56.14, 3.89) * mm});
            skLineSegment(sketch, "E231", {"start": v(-56.14, 3.89) * mm, "end": v(-56.07, 3.77) * mm});
            skLineSegment(sketch, "E232", {"start": v(-56.07, 3.77) * mm, "end": v(-56.03, 3.63) * mm});
            skLineSegment(sketch, "E233", {"start": v(-56.03, 3.63) * mm, "end": v(-56.02, 3.52) * mm});
            skLineSegment(sketch, "E234", {"start": v(-56.02, 3.52) * mm, "end": v(-56.02, 3.48) * mm});
            skLineSegment(sketch, "E235", {"start": v(-56.02, 3.48) * mm, "end": v(-56.02, -1.52) * mm});
            skLineSegment(sketch, "E236", {"start": v(-56.02, -1.52) * mm, "end": v(-56.02, -1.56) * mm});
            skLineSegment(sketch, "E237", {"start": v(-56.02, -1.56) * mm, "end": v(-55.99, -1.67) * mm});
            skLineSegment(sketch, "E238", {"start": v(-55.99, -1.67) * mm, "end": v(-55.9, -1.8) * mm});
            skLineSegment(sketch, "E239", {"start": v(-55.9, -1.8) * mm, "end": v(-55.78, -1.88) * mm});
            skLineSegment(sketch, "E240", {"start": v(-55.78, -1.88) * mm, "end": v(-55.66, -1.9) * mm});
            skLineSegment(sketch, "E241", {"start": v(-55.66, -1.9) * mm, "end": v(-55.62, -1.9) * mm});
            skLineSegment(sketch, "E242", {"start": v(-55.62, -1.9) * mm, "end": v(-55.59, -1.9) * mm});
            skLineSegment(sketch, "E243", {"start": v(-55.59, -1.9) * mm, "end": v(-55.47, -1.88) * mm});
            skLineSegment(sketch, "E244", {"start": v(-55.47, -1.88) * mm, "end": v(-55.35, -1.8) * mm});
            skLineSegment(sketch, "E245", {"start": v(-55.35, -1.8) * mm, "end": v(-55.27, -1.67) * mm});
            skLineSegment(sketch, "E246", {"start": v(-55.27, -1.67) * mm, "end": v(-55.23, -1.56) * mm});
            skLineSegment(sketch, "E247", {"start": v(-55.23, -1.56) * mm, "end": v(-55.23, -1.52) * mm});
            skLineSegment(sketch, "E248", {"start": v(-55.23, -1.52) * mm, "end": v(-55.23, 3.48) * mm});
            skLineSegment(sketch, "E249", {"start": v(-55.23, 3.48) * mm, "end": v(-55.23, 3.56) * mm});
            skLineSegment(sketch, "E250", {"start": v(-55.23, 3.56) * mm, "end": v(-55.27, 3.79) * mm});
            skLineSegment(sketch, "E251", {"start": v(-55.27, 3.79) * mm, "end": v(-55.35, 4.07) * mm});
            skLineSegment(sketch, "E252", {"start": v(-55.35, 4.07) * mm, "end": v(-55.5, 4.33) * mm});
            skLineSegment(sketch, "E253", {"start": v(-55.5, 4.33) * mm, "end": v(-55.68, 4.55) * mm});
            skLineSegment(sketch, "E254", {"start": v(-55.68, 4.55) * mm, "end": v(-55.9, 4.73) * mm});
            skLineSegment(sketch, "E255", {"start": v(-55.9, 4.73) * mm, "end": v(-56.16, 4.87) * mm});
            skLineSegment(sketch, "E256", {"start": v(-56.16, 4.87) * mm, "end": v(-56.44, 4.96) * mm});
            skLineSegment(sketch, "E257", {"start": v(-56.44, 4.96) * mm, "end": v(-56.67, 5) * mm});
            skLineSegment(sketch, "E258", {"start": v(-56.67, 5) * mm, "end": v(-56.74, 5) * mm});
            skLineSegment(sketch, "E259", {"start": v(-56.74, 5) * mm, "end": v(-62.92, 5) * mm});
            skLineSegment(sketch, "E260", {"start": v(-55.21, -3.83) * mm, "end": v(-55.21, -5.18) * mm});
            skLineSegment(sketch, "E261", {"start": v(-55.21, -5.18) * mm, "end": v(-57.08, -3.42) * mm});
            skLineSegment(sketch, "E262", {"start": v(-57.08, -3.42) * mm, "end": v(-55.62, -3.42) * mm});
            skLineSegment(sketch, "E263", {"start": v(-55.62, -3.42) * mm, "end": v(-55.58, -3.42) * mm});
            skLineSegment(sketch, "E264", {"start": v(-55.58, -3.42) * mm, "end": v(-55.46, -3.45) * mm});
            skLineSegment(sketch, "E265", {"start": v(-55.46, -3.45) * mm, "end": v(-55.33, -3.54) * mm});
            skLineSegment(sketch, "E266", {"start": v(-55.33, -3.54) * mm, "end": v(-55.24, -3.67) * mm});
            skLineSegment(sketch, "E267", {"start": v(-55.24, -3.67) * mm, "end": v(-55.21, -3.79) * mm});
            skLineSegment(sketch, "E268", {"start": v(-55.21, -3.79) * mm, "end": v(-55.21, -3.83) * mm});
            skSolve(sketch);
        }
        {
            var Q0;
            Q0 = qSketchRegion(id + "F11", true);
            extrude(context, id + "F12", {"entities" : qUnion([Q0]), "operationType" : NewBodyOperationType.REMOVE, "oppositeDirection" : true, "depth" : 3 * mm, "offsetDistance" : 25 * mm});
        }
        {
            var Q0;
            Q0=makeQuery(id+"F3.opExtrude","CAP_FACE",FACE,{"disambiguationData":[OSD([sQuery(id+"F2.wireOp",EDGE,"E27"),sQuery(id+"F2.wireOp",EDGE,"E28"),sQuery(id+"F2.wireOp",EDGE,"E29"),sQuery(id+"F2.wireOp",EDGE,"E30"),sQuery(id+"F2.wireOp",EDGE,"E31"),sQuery(id+"F2.wireOp",EDGE,"E32.MirrorCS"),sQuery(id+"F2.wireOp",EDGE,"E34.MirrorCS"),sQuery(id+"F2.wireOp",EDGE,"E35.MirrorCS")])],"isStart":false});
            var sketch = newSketch(context, id + "F13", { "sketchPlane" : qUnion([Q0])});
            skLineSegment(sketch, "E269", {"start": v(-61.46, 55.17) * mm, "end": v(-61.46, 47.18) * mm});
            skLineSegment(sketch, "E270", {"start": v(-61.46, 47.18) * mm, "end": v(-54.53, 51.17) * mm});
            skLineSegment(sketch, "E271", {"start": v(-54.53, 51.17) * mm, "end": v(-61.46, 55.17) * mm});
            skLineSegment(sketch, "E272", {"start": v(-60.8, 54.02) * mm, "end": v(-55.85, 51.17) * mm});
            skLineSegment(sketch, "E273", {"start": v(-55.85, 51.17) * mm, "end": v(-60.8, 48.33) * mm});
            skLineSegment(sketch, "E274", {"start": v(-60.8, 48.33) * mm, "end": v(-60.8, 54.02) * mm});
            skLineSegment(sketch, "E275", {"start": v(-63.05, 48.05) * mm, "end": v(-57.63, 51.17) * mm});
            skLineSegment(sketch, "E276", {"start": v(-57.63, 51.17) * mm, "end": v(-63.05, 54.3) * mm});
            skLineSegment(sketch, "E277", {"start": v(-63.05, 54.3) * mm, "end": v(-63.05, 48.05) * mm});
            skLineSegment(sketch, "E278", {"start": v(-62.39, 53.15) * mm, "end": v(-58.96, 51.17) * mm});
            skLineSegment(sketch, "E279", {"start": v(-58.96, 51.17) * mm, "end": v(-62.39, 49.2) * mm});
            skLineSegment(sketch, "E280", {"start": v(-62.39, 49.2) * mm, "end": v(-62.39, 53.15) * mm});
            skSolve(sketch);
        }
        {
            var Q0;
            Q0 = qSketchRegion(id + "F13", true);
            var Q1;
            {var subQ1=sQuery(id+"F13.wireOp",EDGE,"E275");var subQ3=sQuery(id+"F13.wireOp",EDGE,"E274");var subQ4=makeQuery(id+"F13.imprint","INTERSECT",VERTEX,{"derivedFrom":[subQ3,subQ1]});Q1=makeQuery(id+"F13.imprint","IMPRINT",FACE,{"disambiguationData":[TD([[makeQuery(id+"F13.imprint","IMPRINT",EDGE,{"disambiguationData":[TD([[subQ4,-1.0]])],"derivedFrom":subQ3}),-1.0]])]});}
            var Q2;
            {var subQ0=sQuery(id+"F13.wireOp",EDGE,"E278");var subQ1=sQuery(id+"F13.wireOp",EDGE,"E269");var subQ2=makeQuery(id+"F13.imprint","INTERSECT",VERTEX,{"derivedFrom":[subQ1,subQ0]});Q2=makeQuery(id+"F13.imprint","IMPRINT",FACE,{"disambiguationData":[TD([[makeQuery(id+"F13.imprint","IMPRINT",EDGE,{"disambiguationData":[TD([[subQ2,-1.0]])],"derivedFrom":subQ1}),1.0]])]});}
            extrude(context, id + "F14", {"entities" : qUnion([Q0, Q1, Q2]), "operationType" : NewBodyOperationType.REMOVE, "oppositeDirection" : true, "depth" : 3 * mm, "offsetDistance" : 25 * mm});
        }
        {
            var Q0;
            Q0=makeQuery(id+"F5.opPattern","COPY",EDGE,{"derivedFrom":makeQuery(id+"F1.opExtrude","CAP_EDGE",EDGE,{"disambiguationData":[OSD([sQuery(id+"F0.wireOp",EDGE,"E11")])],"isStart":true}),"instanceName":"1"});
            fillet(context, id + "F15", {"entities" : qUnion([Q0]), "radius" : 2 * mm, "tangentPropagation" : true, "allowEdgeOverflow" : false});
        }
        {
            var Q0;
            Q0=makeQuery(id+"F5.opPattern","COPY",EDGE,{"derivedFrom":makeQuery(id+"F1.opExtrude","CAP_EDGE",EDGE,{"disambiguationData":[OSD([sQuery(id+"F0.wireOp",EDGE,"E12")])],"isStart":true}),"instanceName":"1"});
            var Q1;
            Q1=makeQuery(id+"F5.opPattern","COPY",EDGE,{"derivedFrom":makeQuery(id+"F1.opExtrude","CAP_EDGE",EDGE,{"disambiguationData":[OSD([sQuery(id+"F0.wireOp",EDGE,"E16")])],"isStart":false}),"instanceName":"1"});
            fillet(context, id + "F16", {"entities" : qUnion([Q0, Q1]), "radius" : 2 * mm, "tangentPropagation" : true, "allowEdgeOverflow" : false});
        }
    });
